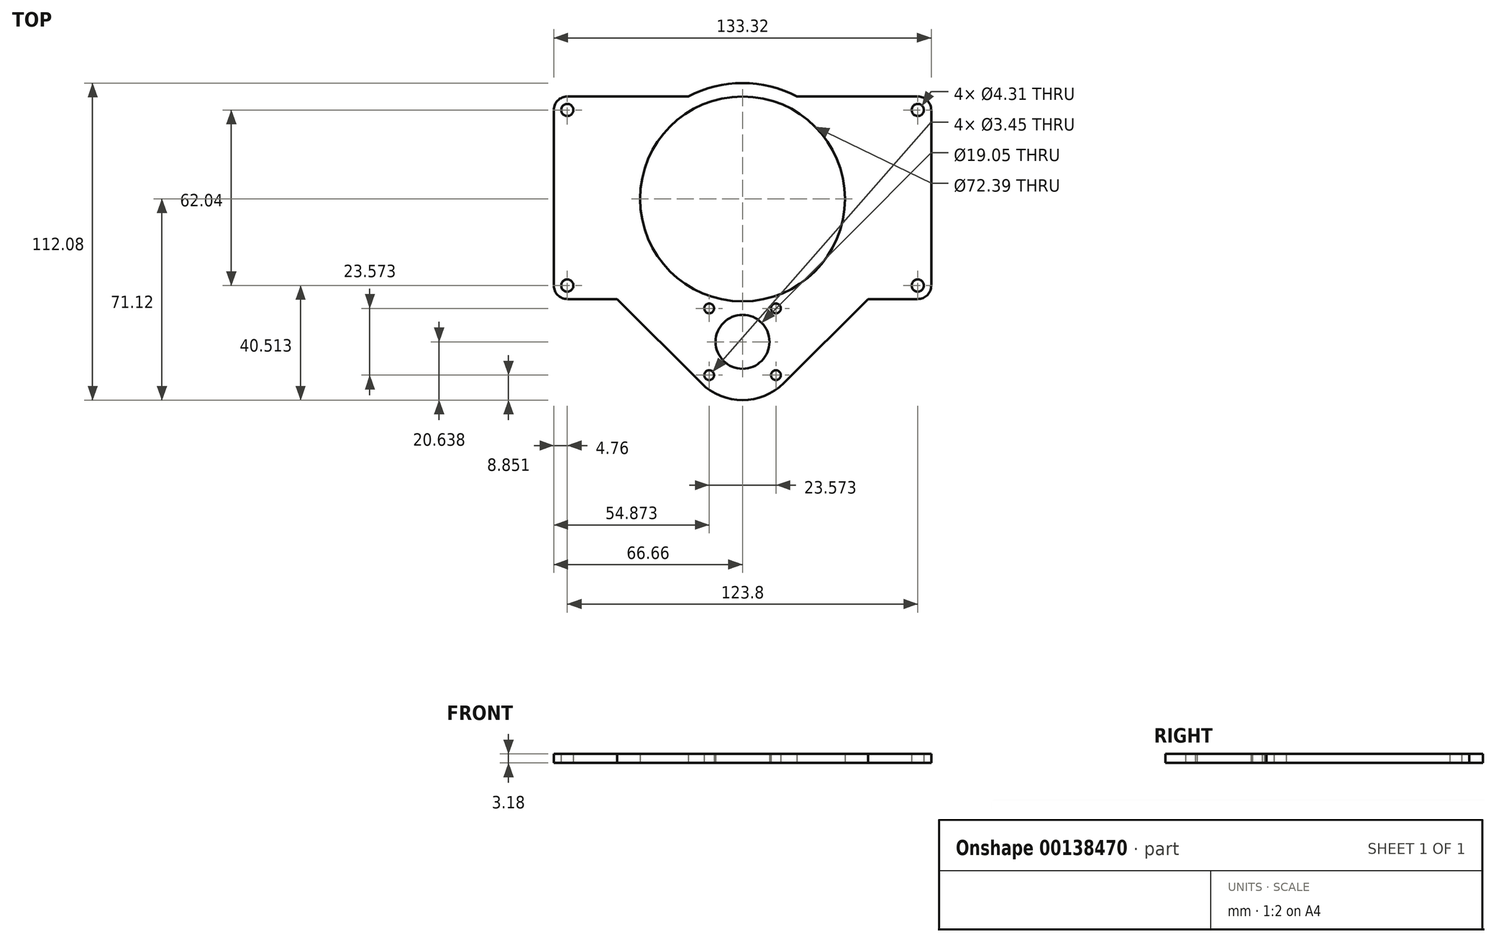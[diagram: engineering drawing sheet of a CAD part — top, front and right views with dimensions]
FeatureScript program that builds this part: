
annotation { "Feature Type Name" : "Feature", "Feature Type Description" : "" }
export const myFeature = defineFeature(function(context is Context, id is Id, definition is map)
    precondition{}
    {
        {
            var Q0;
            Q0=qCreatedBy(makeId("Top.planeOp"),FACE);
            var sketch = newSketch(context, id + "F0", { "sketchPlane" : qUnion([Q0])});
            skPoint(sketch, "E0.middle", {"position": v(0, 0) * mm});
            skLineSegment(sketch, "E1.left", {"start": v(-66.66, 36.2) * mm, "end": v(-66.66, -35.37) * mm});
            skLineSegment(sketch, "E1.right", {"start": v(66.66, 36.2) * mm, "end": v(66.66, -35.37) * mm});
            skLineSegment(sketch, "E2", {"start": v(11.79, -38.7) * mm, "end": v(-11.79, -62.27) * mm, "construction": true});
            skCircle(sketch, "E3", {"center": v(0, -50.48) * mm, "radius": 9.53 * mm});
            skLineSegment(sketch, "E4", {"start": v(-11.79, -38.7) * mm, "end": v(11.79, -62.27) * mm, "construction": true});
            skLineSegment(sketch, "E5", {"start": v(61.9, 31.43) * mm, "end": v(61.9, 36.2) * mm, "construction": true});
            skLineSegment(sketch, "E6", {"start": v(61.9, 31.43) * mm, "end": v(66.66, 31.43) * mm, "construction": true});
            skLineSegment(sketch, "E7", {"start": v(-61.9, 31.43) * mm, "end": v(-66.66, 31.43) * mm, "construction": true});
            skCircle(sketch, "E8", {"center": v(61.9, 31.43) * mm, "radius": 2.15 * mm});
            skCircle(sketch, "E9", {"center": v(-61.9, 31.43) * mm, "radius": 2.15 * mm});
            skCircle(sketch, "E10", {"center": v(11.79, -38.7) * mm, "radius": 1.73 * mm});
            skLineSegment(sketch, "E11", {"start": v(0, 0) * mm, "end": v(0, -50.48) * mm, "construction": true});
            skCircle(sketch, "E12", {"center": v(-11.79, -38.7) * mm, "radius": 1.73 * mm});
            skCircle(sketch, "E13", {"center": v(-11.79, -62.27) * mm, "radius": 1.73 * mm});
            skCircle(sketch, "E14", {"center": v(11.79, -62.27) * mm, "radius": 1.73 * mm});
            skLineSegment(sketch, "E15", {"start": v(-61.9, -30.6) * mm, "end": v(-66.66, -30.6) * mm, "construction": true});
            skLineSegment(sketch, "E16", {"start": v(-61.9, -30.6) * mm, "end": v(-61.9, -35.37) * mm, "construction": true});
            skLineSegment(sketch, "E17", {"start": v(-66.66, -35.37) * mm, "end": v(-44.3, -35.37) * mm});
            skLineSegment(sketch, "E18", {"start": v(66.66, -35.37) * mm, "end": v(44.3, -35.37) * mm});
            skLineSegment(sketch, "E19", {"start": v(-44.3, -35.37) * mm, "end": v(-14.6, -65.08) * mm});
            skLineSegment(sketch, "E20", {"start": v(44.3, -35.37) * mm, "end": v(14.6, -65.08) * mm});
            skArc(sketch, "E21", {"start": v(-14.6, -65.08) * mm, "mid": v(0, -71.12) * mm, "end": v(14.6, -65.08) * mm});
            skCircle(sketch, "E22", {"center": v(11.79, -62.27) * mm, "radius": 3.97 * mm, "construction": true});
            skCircle(sketch, "E23", {"center": v(61.9, -30.6) * mm, "radius": 2.15 * mm});
            skCircle(sketch, "E24", {"center": v(-61.9, -30.6) * mm, "radius": 2.15 * mm});
            skCircle(sketch, "E25", {"center": v(0, 0) * mm, "radius": 36.2 * mm});
            skArc(sketch, "E26", {"start": v(19.17, 36.2) * mm, "mid": v(0, 40.96) * mm, "end": v(-19.17, 36.2) * mm});
            skLineSegment(sketch, "E27", {"start": v(-66.66, 36.2) * mm, "end": v(-19.17, 36.2) * mm});
            skLineSegment(sketch, "E28", {"start": v(66.66, 36.2) * mm, "end": v(19.17, 36.2) * mm});
            skLineSegment(sketch, "E29", {"start": v(61.9, -30.6) * mm, "end": v(66.66, -30.6) * mm, "construction": true});
            skSolve(sketch);
        }
        {
            var Q0;
            Q0=qSketchRegion(id+"F0",true);
            extrude(context, id + "F1", {"entities" : qUnion([Q0]), "depth" : 3.17 * mm});
        }
        {
            var Q0;
            Q0=makeQuery(id+"F1.opExtrude","SWEPT_EDGE",EDGE,{"disambiguationData":[OSD([sQuery(id+"F0.wireOp",EDGE,"E1.bottom"),sQuery(id+"F0.wireOp",EDGE,"E1.left")])]});
            var Q1;
            Q1=makeQuery(id+"F1.opExtrude","SWEPT_EDGE",EDGE,{"disambiguationData":[OSD([sQuery(id+"F0.wireOp",EDGE,"E1.bottom"),sQuery(id+"F0.wireOp",EDGE,"E1.right")])]});
            var Q2;
            Q2=makeQuery(id+"F1.opExtrude","SWEPT_EDGE",EDGE,{"disambiguationData":[OSD([sQuery(id+"F0.wireOp",EDGE,"E1.right"),sQuery(id+"F0.wireOp",EDGE,"E18")])]});
            var Q3;
            Q3=makeQuery(id+"F1.opExtrude","SWEPT_EDGE",EDGE,{"disambiguationData":[OSD([sQuery(id+"F0.wireOp",EDGE,"E1.left"),sQuery(id+"F0.wireOp",EDGE,"E17")])]});
            fillet(context, id + "F2", {"entities" : qUnion([Q0, Q1, Q2, Q3]), "radius" : 4.76 * mm, "tangentPropagation" : true, "allowEdgeOverflow" : false});
        }
    });
